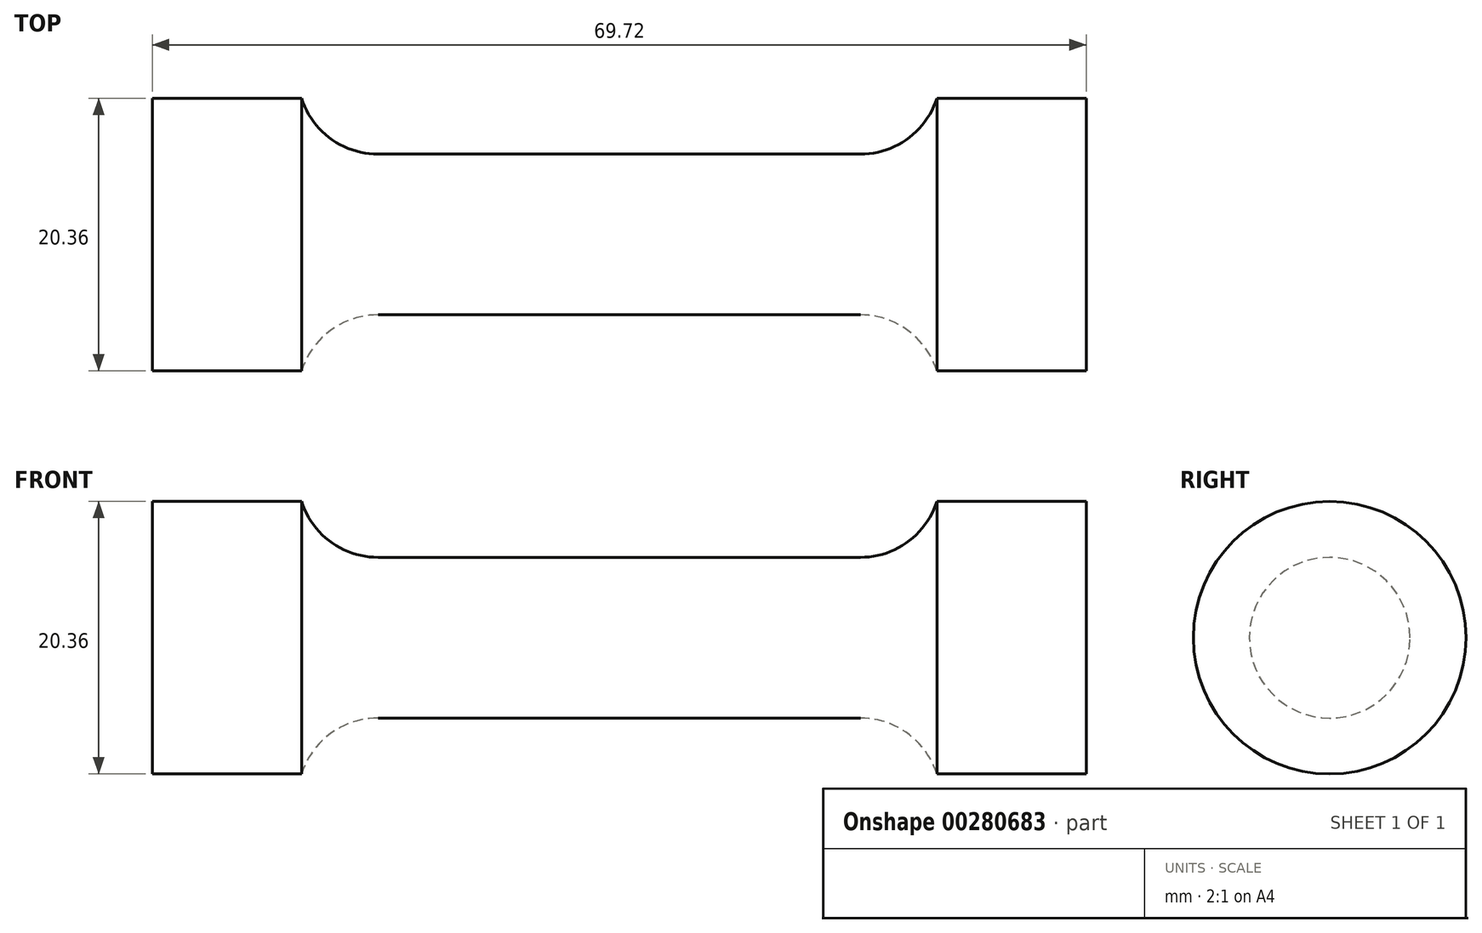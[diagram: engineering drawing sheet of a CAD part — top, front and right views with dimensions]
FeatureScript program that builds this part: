
annotation { "Feature Type Name" : "Feature", "Feature Type Description" : "" }
export const myFeature = defineFeature(function(context is Context, id is Id, definition is map)
    precondition{}
    {
        {
            var Q0;
            Q0=qCreatedBy(makeId("Front.planeOp"),FACE);
            var sketch = newSketch(context, id + "F0", { "sketchPlane" : qUnion([Q0])});
            skLineSegment(sketch, "E0", {"start": v(0, 6) * mm, "end": v(18, 6) * mm});
            skArc(sketch, "E1", {"start": v(18, 6) * mm, "mid": v(21.54, 7.16) * mm, "end": v(23.72, 10.18) * mm});
            skLineSegment(sketch, "E2", {"start": v(23.72, 10.18) * mm, "end": v(34.86, 10.18) * mm});
            skLineSegment(sketch, "E3", {"start": v(34.86, 10.18) * mm, "end": v(34.86, 0) * mm});
            skLineSegment(sketch, "E4.MirrorCS", {"start": v(0, 6) * mm, "end": v(-18, 6) * mm});
            skArc(sketch, "E5.MirrorCS", {"start": v(-18, 6) * mm, "mid": v(-21.54, 7.16) * mm, "end": v(-23.72, 10.18) * mm});
            skLineSegment(sketch, "E6.MirrorCS", {"start": v(-23.72, 10.18) * mm, "end": v(-34.86, 10.18) * mm});
            skLineSegment(sketch, "E7.MirrorCS", {"start": v(-34.86, 10.18) * mm, "end": v(-34.86, 0) * mm});
            skLineSegment(sketch, "E8", {"start": v(-34.86, 0) * mm, "end": v(34.86, 0) * mm});
            skSolve(sketch);
        }
        {
            var Q0;
            Q0=makeQuery(id+"F0.imprint","IMPRINT",FACE,{"disambiguationData":[TD([[makeQuery(id+"F0.imprint","IMPRINT",EDGE,{"derivedFrom":sQuery(id+"F0.wireOp",EDGE,"E0")}),-1.0]])]});
            var Q1;
            Q1=sQuery(id+"F0.wireOp",EDGE,"E8");
            revolve(context, id + "F1", {"entities" : qUnion([Q0]), "axis" : qUnion([Q1]), "revolveType" : RevolveType.FULL});
        }
    });
